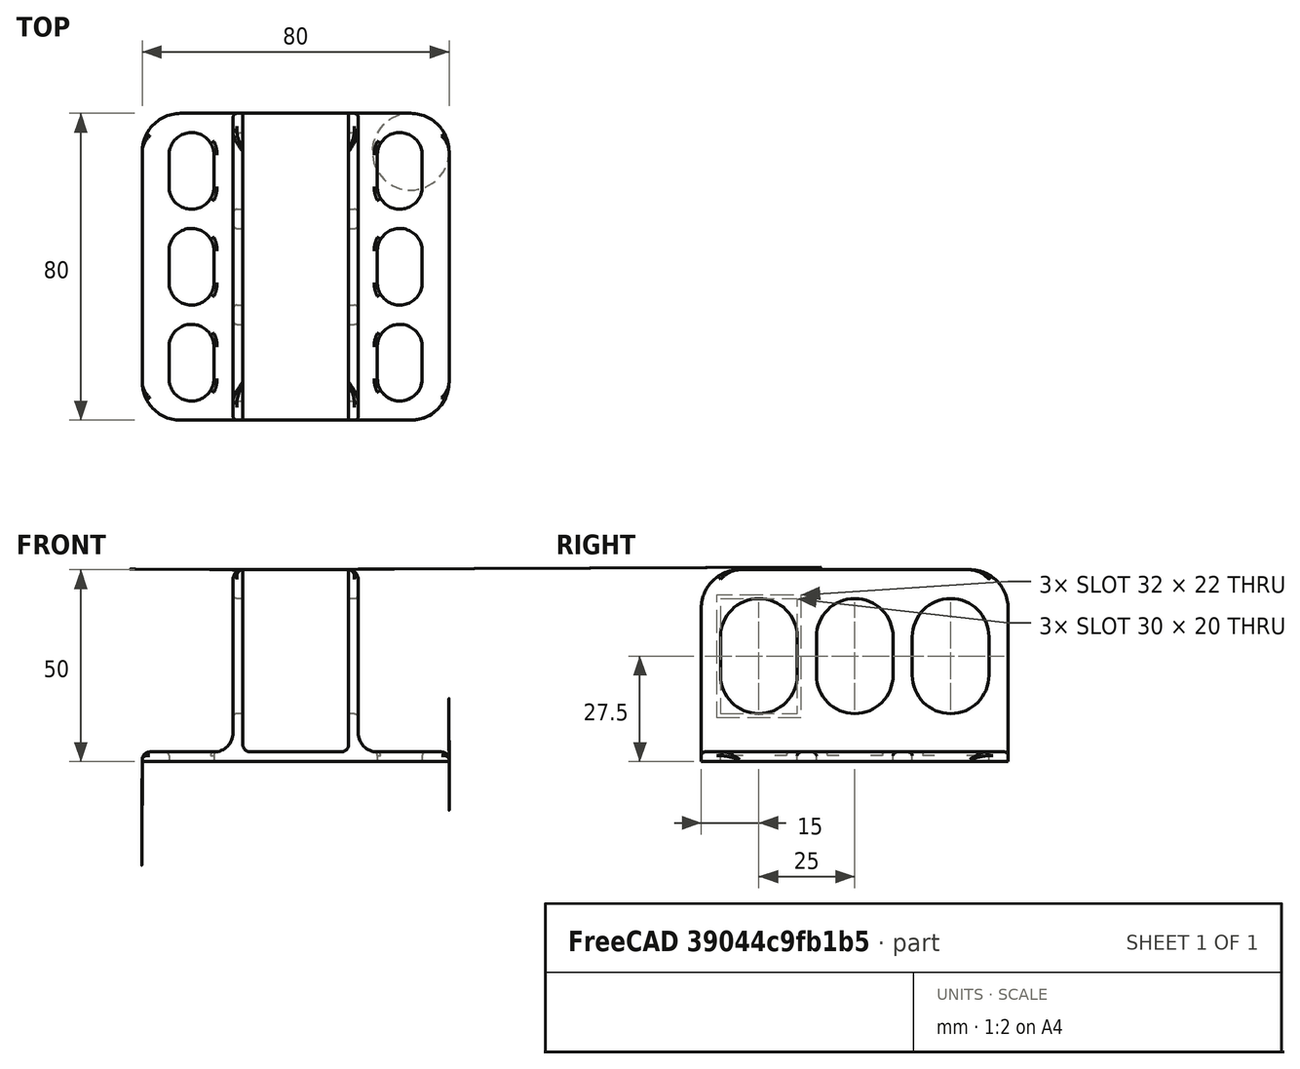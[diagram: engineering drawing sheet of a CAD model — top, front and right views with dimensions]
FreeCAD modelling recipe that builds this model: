
FCSTD DOCUMENT  (FreeCAD 1.0R39319 (Git))
Label: Charger Stand-2.1
License: Creative Commons Attribution 4.0
LicenseURL: https://creativecommons.org/licenses/by/4.0/
objects: Sketcher::SketchObject×5, PartDesign::Pocket×4, PartDesign::Pad×1, PartDesign::Fillet×1, PartDesign::Body×1
note: 29 computed .brp shape members not serialized (recipe doc carries the construction recipe); baked Part::Feature solids carry a one-line shape summary decoded from their .brp

FEATURE [Sketcher::SketchObject] Sketch
  ArcFitTolerance = 1e-06
  AttachmentSupport = -> [XZ_Plane]
  FullyConstrained = true
  MakeInternals = false
  MapMode = 5
  Placement = pos=(0,0,0) rot=(1,0,0;1.5708rad)
  sketch-geometry (18):
    g0: LineSegment StartX=-40 StartY=0 StartZ=0 EndX=40 EndY=0 EndZ=0
    g1: LineSegment StartX=38 StartY=2.5 StartZ=0 EndX=21.3 EndY=2.5 EndZ=0
    g2: LineSegment StartX=-38 StartY=2.5 StartZ=0 EndX=-21.3 EndY=2.5 EndZ=0
    g3: LineSegment StartX=-16.3 StartY=7.5 StartZ=0 EndX=-16.3 EndY=47.5 EndZ=0
    g4: LineSegment StartX=-13.8 StartY=50 StartZ=0 EndX=-13.8 EndY=4.5 EndZ=0
    g5: LineSegment StartX=-11.8 StartY=2.5 StartZ=0 EndX=11.8 EndY=2.5 EndZ=0
    g6: LineSegment StartX=13.8 StartY=4.5 StartZ=0 EndX=13.8 EndY=50 EndZ=0
    g7: LineSegment StartX=16.3 StartY=47.5 StartZ=0 EndX=16.3 EndY=7.5 EndZ=0
    g8: ArcOfCircle CenterX=-13.8 CenterY=47.5 CenterZ=0 NormalX=0 NormalY=0 NormalZ=1 AngleXU=0 Radius=2.5 StartAngle=1.5708 EndAngle=3.14159
    g9: ArcOfCircle CenterX=13.8 CenterY=47.5 CenterZ=0 NormalX=0 NormalY=0 NormalZ=1 AngleXU=0 Radius=2.5 StartAngle=-9e-16 EndAngle=1.5708
    g10: ArcOfCircle CenterX=21.3 CenterY=7.5 CenterZ=0 NormalX=0 NormalY=0 NormalZ=1 AngleXU=0 Radius=5 StartAngle=3.14159 EndAngle=4.71239
    g11: ArcOfCircle CenterX=11.8 CenterY=4.5 CenterZ=0 NormalX=0 NormalY=0 NormalZ=1 AngleXU=0 Radius=2 StartAngle=4.71239 EndAngle=6.28319
    g12: ArcOfCircle CenterX=-11.8 CenterY=4.5 CenterZ=0 NormalX=0 NormalY=0 NormalZ=1 AngleXU=0 Radius=2 StartAngle=3.14159 EndAngle=4.71239
    g13: ArcOfCircle CenterX=-21.3 CenterY=7.5 CenterZ=0 NormalX=0 NormalY=0 NormalZ=1 AngleXU=0 Radius=5 StartAngle=4.71239 EndAngle=6.28319
    g14: LineSegment StartX=40 StartY=0 StartZ=0 EndX=40 EndY=0.5 EndZ=0
    g15: LineSegment StartX=-40 StartY=0 StartZ=0 EndX=-40 EndY=0.5 EndZ=0
    g16: ArcOfCircle CenterX=38 CenterY=0.5 CenterZ=0 NormalX=0 NormalY=0 NormalZ=1 AngleXU=0 Radius=2 StartAngle=0 EndAngle=1.5708
    g17: ArcOfCircle CenterX=-38 CenterY=0.5 CenterZ=0 NormalX=0 NormalY=0 NormalZ=1 AngleXU=0 Radius=2 StartAngle=1.5708 EndAngle=3.14159
  constraints (47):
    c: PointOnObject(g0,g-1)
    c: Horizontal(g1)
    c: Horizontal(g2)
    c: Vertical(g3)
    c: Vertical(g4)
    c: Horizontal(g5)
    c: Vertical(g6)
    c: Vertical(g7)
    c: Coincident(g8,g4)
    c: Coincident(g9,g6)
    c: Symmetric(g0,g0,g-2)
    c: Tangent(g10,g1) = 1.5708
    c: Tangent(g10,g7) = -1.5708
    c: Tangent(g11,g6) = -1.5708
    c: Tangent(g11,g5) = -1.5708
    c: Tangent(g12,g5) = -1.5708
    c: Tangent(g12,g4) = -1.5708
    c: Tangent(g13,g3) = -1.5708
    c: Tangent(g13,g2) = -1.5708
    c: Tangent(g8,g3) = 1.5708
    c: Perpendicular(g8,g4)
    c: Perpendicular(g9,g6)
    c: Tangent(g9,g7) = 1.5708
    c: Coincident(g14,g0)
    c: Coincident(g15,g0)
    c: Vertical(g15)
    c: Tangent(g17,g15) = 1.5708
    c: Tangent(g17,g2) = 1.5708
    c: Tangent(g16,g14) = -1.5708
    c: Tangent(g16,g1) = -1.5708
    c: Vertical(g14)
    c: Equal(g14,g15)
    c: Equal(g17,g12)
    c: Equal(g12,g11)
    c: Equal(g11,g16)
    c: Equal(g8,g9)
    c: Equal(g2,g1)
    c: Equal(g7,g3)
    c: Equal(g4,g6)
    c: Radius(g16) = 2
    c: DistanceY(g1) = 2.5
    c: DistanceX(g4,g6) = 27.6
    c: Radius(g9) = 2.5
    c: Radius(g10) = 5
    c: Horizontal(g5,g1)
    c: DistanceY(g6) = 50
    c: DistanceX(g0,g0) = 80
FEATURE [PartDesign::Pad] Pad
  Direction = (0,-1,2e-16)
  Length = 80
  Length2 = 10
  Midplane = true
  Placement = pos=(0,0,0) rot=(1,0,0;1.5708rad)
  Profile = -> Sketch
  ReferenceAxis = -> Sketch [N_Axis]
  Refine = true
  Suppressed = false
  Type = 0
FEATURE [Sketcher::SketchObject] Sketch001
  ArcFitTolerance = 1e-06
  AttachmentSupport = -> [Pad]
  ExternalGeometry = -> [Pad]
  FullyConstrained = true
  MakeInternals = false
  MapMode = 5
  Placement = pos=(16.3,0,0) rot=(0.707107,0,0.707107;3.14159rad)
  sketch-geometry (6):
    g0: LineSegment StartX=50 StartY=40 StartZ=0 EndX=40 EndY=40 EndZ=0
    g1: LineSegment StartX=50 StartY=40 StartZ=0 EndX=50 EndY=30 EndZ=0
    g2: LineSegment StartX=50 StartY=-40 StartZ=0 EndX=50 EndY=-30 EndZ=0
    g3: LineSegment StartX=50 StartY=-40 StartZ=0 EndX=40 EndY=-40 EndZ=0
    g4: ArcOfCircle CenterX=40 CenterY=30 CenterZ=0 NormalX=0 NormalY=0 NormalZ=1 AngleXU=0 Radius=10 StartAngle=0 EndAngle=1.5708
    g5: ArcOfCircle CenterX=40 CenterY=-30 CenterZ=0 NormalX=0 NormalY=0 NormalZ=1 AngleXU=0 Radius=10 StartAngle=4.71239 EndAngle=6.28319
  constraints (17):
    c: Coincident(g0,g-3)
    c: Horizontal(g0)
    c: Coincident(g1,g0)
    c: PointOnObject(g1,g-3)
    c: Coincident(g2,g-3)
    c: PointOnObject(g2,g-3)
    c: Coincident(g3,g2)
    c: Horizontal(g3)
    c: Equal(g2,g3)
    c: Equal(g3,g1)
    c: Equal(g1,g0)
    c: Coincident(g4,g0)
    c: Coincident(g5,g2)
    c: Coincident(g5,g3)
    c: Tangent(g4,g1) = 1.5708
    c: Radius(g4) = 10
    c: Equal(g5,g4)
FEATURE [PartDesign::Pocket] Pocket
  BaseFeature = -> Pad
  Direction = (-1,0,2e-16)
  Length = 5
  Length2 = 5
  Placement = pos=(0,0,0) rot=(1,0,0;1.5708rad)
  Profile = -> Sketch001
  ReferenceAxis = -> Sketch001 [N_Axis]
  Refine = true
  Suppressed = false
  Type = 1
FEATURE [Sketcher::SketchObject] Sketch002
  ArcFitTolerance = 1e-06
  AttachmentSupport = -> [Pocket]
  ExternalGeometry = -> [Pocket]
  FullyConstrained = true
  MakeInternals = false
  MapMode = 5
  Placement = pos=(0,1.1e-15,2.5) rot=(0,0,1;3.14159rad)
  sketch-geometry (12):
    g0: LineSegment StartX=-40 StartY=30 StartZ=0 EndX=-40 EndY=40 EndZ=0
    g1: LineSegment StartX=-40 StartY=40 StartZ=0 EndX=-30 EndY=40 EndZ=0
    g2: LineSegment StartX=30 StartY=40 StartZ=0 EndX=40 EndY=40 EndZ=0
    g3: LineSegment StartX=40 StartY=40 StartZ=0 EndX=40 EndY=30 EndZ=0
    g4: LineSegment StartX=40 StartY=-30 StartZ=0 EndX=40 EndY=-40 EndZ=0
    g5: LineSegment StartX=40 StartY=-40 StartZ=0 EndX=30 EndY=-40 EndZ=0
    g6: LineSegment StartX=-40 StartY=-40 StartZ=0 EndX=-40 EndY=-30 EndZ=0
    g7: LineSegment StartX=-40 StartY=-40 StartZ=0 EndX=-30 EndY=-40 EndZ=0
    g8: ArcOfCircle CenterX=-30 CenterY=30 CenterZ=0 NormalX=0 NormalY=0 NormalZ=1 AngleXU=0 Radius=10 StartAngle=1.5708 EndAngle=3.14159
    g9: ArcOfCircle CenterX=30 CenterY=30 CenterZ=0 NormalX=0 NormalY=0 NormalZ=1 AngleXU=0 Radius=10 StartAngle=3e-16 EndAngle=1.5708
    g10: ArcOfCircle CenterX=30 CenterY=-30 CenterZ=0 NormalX=0 NormalY=0 NormalZ=1 AngleXU=0 Radius=10 StartAngle=4.71239 EndAngle=6.28319
    g11: ArcOfCircle CenterX=-30 CenterY=-30 CenterZ=0 NormalX=0 NormalY=0 NormalZ=1 AngleXU=0 Radius=10 StartAngle=3.14159 EndAngle=4.71239
  constraints (35):
    c: PointOnObject(g0,g-4)
    c: Coincident(g0,g-4)
    c: Coincident(g1,g0)
    c: Horizontal(g1)
    c: Coincident(g2,g-3)
    c: Horizontal(g2)
    c: Coincident(g3,g2)
    c: PointOnObject(g3,g-3)
    c: PointOnObject(g4,g-3)
    c: Coincident(g4,g-3)
    c: Coincident(g5,g4)
    c: Horizontal(g5)
    c: Coincident(g6,g-4)
    c: PointOnObject(g6,g-4)
    c: Coincident(g7,g6)
    c: Horizontal(g7)
    c: Equal(g7,g6)
    c: Equal(g6,g0)
    c: Equal(g0,g1)
    c: Equal(g1,g2)
    c: Equal(g2,g3)
    c: Equal(g3,g4)
    c: Equal(g4,g5)
    c: Coincident(g8,g0)
    c: Coincident(g8,g1)
    c: Coincident(g9,g2)
    c: Coincident(g9,g3)
    c: Coincident(g10,g5)
    c: Coincident(g11,g6)
    c: Coincident(g11,g7)
    c: Equal(g11,g8)
    c: Equal(g8,g9)
    c: Equal(g9,g10)
    c: Tangent(g10,g4) = 1.5708
    c: Radius(g9) = 10
FEATURE [PartDesign::Pocket] Pocket001
  BaseFeature = -> Pocket
  Direction = (0,0,-1)
  Length = 5
  Length2 = 5
  Placement = pos=(0,0,0) rot=(1,0,0;1.5708rad)
  Profile = -> Sketch002
  ReferenceAxis = -> Sketch002 [N_Axis]
  Refine = true
  Suppressed = false
  Type = 1
FEATURE [Sketcher::SketchObject] Sketch003
  ArcFitTolerance = 1e-06
  AttachmentSupport = -> [Pocket001]
  ExternalGeometry = -> [Pocket001]
  FullyConstrained = true
  MakeInternals = false
  MapMode = 5
  Placement = pos=(-16.3,0,0) rot=(0.707107,0,-0.707107;3.14159rad)
  sketch-geometry (17):
    g0: ArcOfCircle CenterX=-32.5 CenterY=25 CenterZ=0 NormalX=0 NormalY=0 NormalZ=1 AngleXU=0 Radius=10 StartAngle=1.5708 EndAngle=4.71239
    g1: ArcOfCircle CenterX=-22.5 CenterY=25 CenterZ=0 NormalX=0 NormalY=0 NormalZ=1 AngleXU=0 Radius=10 StartAngle=4.71239 EndAngle=7.85398
    g2: LineSegment StartX=-32.5 StartY=35 StartZ=0 EndX=-22.5 EndY=35 EndZ=0
    g3: LineSegment StartX=-32.5 StartY=15 StartZ=0 EndX=-22.5 EndY=15 EndZ=0
    g4: ArcOfCircle CenterX=-32.5 CenterY=0 CenterZ=0 NormalX=0 NormalY=0 NormalZ=1 AngleXU=0 Radius=10 StartAngle=1.5708 EndAngle=4.71239
    g5: ArcOfCircle CenterX=-22.5 CenterY=-9e-16 CenterZ=0 NormalX=0 NormalY=0 NormalZ=1 AngleXU=0 Radius=10 StartAngle=4.71239 EndAngle=7.85398
    g6: LineSegment StartX=-32.5 StartY=10 StartZ=0 EndX=-22.5 EndY=10 EndZ=0
    g7: LineSegment StartX=-32.5 StartY=-10 StartZ=0 EndX=-22.5 EndY=-10 EndZ=0
    g8: ArcOfCircle CenterX=-32.5 CenterY=-25 CenterZ=0 NormalX=0 NormalY=0 NormalZ=1 AngleXU=0 Radius=10 StartAngle=1.5708 EndAngle=4.71239
    g9: ArcOfCircle CenterX=-22.5 CenterY=-25 CenterZ=0 NormalX=0 NormalY=0 NormalZ=1 AngleXU=0 Radius=10 StartAngle=4.71239 EndAngle=7.85398
    g10: LineSegment StartX=-32.5 StartY=-15 StartZ=0 EndX=-22.5 EndY=-15 EndZ=0
    g11: LineSegment StartX=-32.5 StartY=-35 StartZ=0 EndX=-22.5 EndY=-35 EndZ=0
    g12: LineSegment [constr] StartX=-22.5 StartY=-9e-16 StartZ=0 EndX=-7.5 EndY=-9e-16 EndZ=0
    g13: LineSegment [constr] StartX=-32.5 StartY=0 StartZ=0 EndX=-47.5 EndY=0 EndZ=0
    g14: LineSegment [constr] StartX=-32.5 StartY=10 StartZ=0 EndX=-32.5 EndY=15 EndZ=0
    g15: LineSegment [constr] StartX=-32.5 StartY=35 StartZ=0 EndX=-32.5 EndY=40 EndZ=0
    g16: LineSegment [constr] StartX=-12.5 StartY=25 StartZ=0 EndX=-7.5 EndY=25 EndZ=0
  constraints (44):
    c: Tangent(g0,g2) = 1.5708
    c: Tangent(g0,g3) = -1.5708
    c: Tangent(g1,g2) = 1.5708
    c: Tangent(g1,g3) = -1.5708
    c: Equal(g0,g1)
    c: Horizontal(g2)
    c: Tangent(g4,g6) = 1.5708
    c: Tangent(g4,g7) = -1.5708
    c: Tangent(g5,g6) = 1.5708
    c: Tangent(g5,g7) = -1.5708
    c: Equal(g4,g5)
    c: Horizontal(g7)
    c: PointOnObject(g4,g-1)
    c: Tangent(g8,g10) = 1.5708
    c: Tangent(g8,g11) = -1.5708
    c: Tangent(g9,g10) = 1.5708
    c: Tangent(g9,g11) = -1.5708
    c: Equal(g8,g9)
    c: Equal(g5,g1)
    c: Equal(g1,g9)
    c: Vertical(g9,g5)
    c: Vertical(g8,g4)
    c: Vertical(g4,g0)
    c: Horizontal(g11)
    c: Coincident(g12,g5)
    c: PointOnObject(g12,g-5)
    c: Coincident(g13,g4)
    c: PointOnObject(g13,g-4)
    c: Coincident(g14,g4)
    c: Coincident(g14,g0)
    c: Coincident(g15,g0)
    c: PointOnObject(g15,g-3)
    c: Vertical(g15)
    c: Equal(g14,g15)
    c: Horizontal(g12)
    c: Horizontal(g13)
    c: Equal(g13,g12)
    c: Symmetric(g1,g9,g-1)
    c: DistanceY(g15,g15) = 5
    c: PointOnObject(g16,g1)
    c: PointOnObject(g16,g-5)
    c: Horizontal(g16)
    c: Perpendicular(g1,g16)
    c: Equal(g16,g15)
FEATURE [PartDesign::Pocket] Pocket002
  BaseFeature = -> Pocket001
  Direction = (1,0,2e-16)
  Length = 5
  Length2 = 5
  Placement = pos=(0,0,0) rot=(1,0,0;1.5708rad)
  Profile = -> Sketch003
  ReferenceAxis = -> Sketch003 [N_Axis]
  Refine = true
  Suppressed = false
  Type = 1
FEATURE [Sketcher::SketchObject] Sketch004
  ArcFitTolerance = 1e-06
  AttachmentSupport = -> [Pocket002]
  ExternalGeometry = -> [Pocket002]
  FullyConstrained = true
  MakeInternals = false
  MapMode = 5
  Placement = pos=(0,1.1e-15,2.5) rot=(0,0,1;3.14159rad)
  sketch-geometry (28):
    g0: ArcOfCircle CenterX=-27.15 CenterY=29.15 CenterZ=0 NormalX=0 NormalY=0 NormalZ=1 AngleXU=0 Radius=5.85 StartAngle=4e-16 EndAngle=3.14159
    g1: ArcOfCircle CenterX=-27.15 CenterY=20.85 CenterZ=0 NormalX=0 NormalY=0 NormalZ=1 AngleXU=0 Radius=5.85 StartAngle=3.14159 EndAngle=6.28319
    g2: LineSegment StartX=-21.3 StartY=29.15 StartZ=0 EndX=-21.3 EndY=20.85 EndZ=0
    g3: LineSegment StartX=-33 StartY=29.15 StartZ=0 EndX=-33 EndY=20.85 EndZ=0
    g4: ArcOfCircle CenterX=27.15 CenterY=29.15 CenterZ=0 NormalX=0 NormalY=0 NormalZ=1 AngleXU=0 Radius=5.85 StartAngle=0 EndAngle=3.14159
    g5: ArcOfCircle CenterX=27.15 CenterY=20.85 CenterZ=0 NormalX=0 NormalY=0 NormalZ=1 AngleXU=0 Radius=5.85 StartAngle=3.14159 EndAngle=6.28319
    g6: LineSegment StartX=33 StartY=29.15 StartZ=0 EndX=33 EndY=20.85 EndZ=0
    g7: LineSegment StartX=21.3 StartY=29.15 StartZ=0 EndX=21.3 EndY=20.85 EndZ=0
    g8: LineSegment [constr] StartX=33 StartY=29.15 StartZ=0 EndX=38 EndY=29.15 EndZ=0
    g9: LineSegment [constr] StartX=21.3 StartY=29.15 StartZ=0 EndX=16.3 EndY=29.15 EndZ=0
    g10: LineSegment [constr] StartX=27.15 StartY=35 StartZ=0 EndX=27.15 EndY=40 EndZ=0
    g11: ArcOfCircle CenterX=-27.15 CenterY=4.15 CenterZ=0 NormalX=0 NormalY=0 NormalZ=1 AngleXU=0 Radius=5.85 StartAngle=1e-16 EndAngle=3.14159
    g12: ArcOfCircle CenterX=-27.15 CenterY=-4.15 CenterZ=0 NormalX=0 NormalY=0 NormalZ=1 AngleXU=0 Radius=5.85 StartAngle=3.14159 EndAngle=6.28319
    g13: LineSegment StartX=-21.3 StartY=4.15 StartZ=0 EndX=-21.3 EndY=-4.15 EndZ=0
    g14: LineSegment StartX=-33 StartY=4.15 StartZ=0 EndX=-33 EndY=-4.15 EndZ=0
    g15: ArcOfCircle CenterX=-27.15 CenterY=-20.85 CenterZ=0 NormalX=0 NormalY=0 NormalZ=1 AngleXU=0 Radius=5.85 StartAngle=-9e-16 EndAngle=3.14159
    g16: ArcOfCircle CenterX=-27.15 CenterY=-29.15 CenterZ=0 NormalX=0 NormalY=0 NormalZ=1 AngleXU=0 Radius=5.85 StartAngle=3.14159 EndAngle=6.28319
    g17: LineSegment StartX=-21.3 StartY=-20.85 StartZ=0 EndX=-21.3 EndY=-29.15 EndZ=0
    g18: LineSegment StartX=-33 StartY=-20.85 StartZ=0 EndX=-33 EndY=-29.15 EndZ=0
    g19: ArcOfCircle CenterX=27.15 CenterY=4.15 CenterZ=0 NormalX=0 NormalY=0 NormalZ=1 AngleXU=0 Radius=5.85 StartAngle=1e-16 EndAngle=3.14159
    g20: ArcOfCircle CenterX=27.15 CenterY=-4.15 CenterZ=0 NormalX=0 NormalY=0 NormalZ=1 AngleXU=0 Radius=5.85 StartAngle=3.14159 EndAngle=6.28319
    g21: LineSegment StartX=33 StartY=4.15 StartZ=0 EndX=33 EndY=-4.15 EndZ=0
    g22: LineSegment StartX=21.3 StartY=4.15 StartZ=0 EndX=21.3 EndY=-4.15 EndZ=0
    g23: ArcOfCircle CenterX=27.15 CenterY=-20.85 CenterZ=0 NormalX=0 NormalY=0 NormalZ=1 AngleXU=0 Radius=5.85 StartAngle=0 EndAngle=3.14159
    g24: ArcOfCircle CenterX=27.15 CenterY=-29.15 CenterZ=0 NormalX=0 NormalY=0 NormalZ=1 AngleXU=0 Radius=5.85 StartAngle=3.14159 EndAngle=6.28319
    g25: LineSegment StartX=33 StartY=-20.85 StartZ=0 EndX=33 EndY=-29.15 EndZ=0
    g26: LineSegment StartX=21.3 StartY=-20.85 StartZ=0 EndX=21.3 EndY=-29.15 EndZ=0
    g27: LineSegment [constr] StartX=27.15 StartY=10 StartZ=0 EndX=27.15 EndY=15 EndZ=0
  constraints (67):
    c: Tangent(g0,g2) = 1.5708
    c: Tangent(g0,g3) = -1.5708
    c: Tangent(g1,g2) = 1.5708
    c: Tangent(g1,g3) = -1.5708
    c: Equal(g0,g1)
    c: Vertical(g3)
    c: Tangent(g4,g6) = 1.5708
    c: Tangent(g4,g7) = -1.5708
    c: Tangent(g5,g6) = 1.5708
    c: Tangent(g5,g7) = -1.5708
    c: Equal(g4,g5)
    c: Symmetric(g4,g0,g-2)
    c: Equal(g0,g4)
    c: Horizontal(g1,g5)
    c: Coincident(g8,g4)
    c: PointOnObject(g8,g-3)
    c: Coincident(g9,g4)
    c: PointOnObject(g9,g-4)
    c: Horizontal(g9)
    c: Horizontal(g8)
    c: PointOnObject(g10,g4)
    c: Vertical(g10)
    c: Perpendicular(g4,g10)
    c: Horizontal(g10,g-4)
    c: Equal(g9,g8)
    c: Equal(g8,g10)
    c: DistanceX(g8,g8) = 5
    c: Vertical(g7)
    c: Tangent(g11,g13) = 1.5708
    c: Tangent(g11,g14) = -1.5708
    c: Tangent(g12,g13) = 1.5708
    c: Tangent(g12,g14) = -1.5708
    c: Equal(g11,g12)
    c: Tangent(g15,g17) = 1.5708
    c: Tangent(g15,g18) = -1.5708
    c: Tangent(g16,g17) = 1.5708
    c: Tangent(g16,g18) = -1.5708
    c: Equal(g15,g16)
    c: Tangent(g19,g21) = 1.5708
    c: Tangent(g19,g22) = -1.5708
    c: Tangent(g20,g21) = 1.5708
    c: Tangent(g20,g22) = -1.5708
    c: Equal(g19,g20)
    c: Tangent(g23,g25) = 1.5708
    c: Tangent(g23,g26) = -1.5708
    c: Tangent(g24,g25) = 1.5708
    c: Tangent(g24,g26) = -1.5708
    c: Equal(g23,g24)
    c: Equal(g5,g19)
    c: Equal(g19,g11)
    c: Equal(g11,g15)
    c: Equal(g15,g23)
    c: Vertical(g25)
    c: Vertical(g15,g12)
    c: Symmetric(g19,g11,g-2)
    c: Symmetric(g20,g12,g-2)
    c: Symmetric(g15,g23,g-2)
    c: Symmetric(g16,g24,g-2)
    c: Symmetric(g20,g19,g-1)
    c: PointOnObject(g27,g19)
    c: PointOnObject(g27,g5)
    c: Vertical(g27)
    c: Perpendicular(g19,g27)
    c: Equal(g27,g8)
    c: Equal(g25,g21)
    c: Equal(g21,g6)
    c: Symmetric(g23,g5,g-1)
FEATURE [PartDesign::Pocket] Pocket003
  BaseFeature = -> Pocket002
  Direction = (0,0,-1)
  Length = 5
  Length2 = 5
  Placement = pos=(0,0,0) rot=(1,0,0;1.5708rad)
  Profile = -> Sketch004
  ReferenceAxis = -> Sketch004 [N_Axis]
  Refine = true
  Suppressed = false
  Type = 1
FEATURE [PartDesign::Fillet] Fillet
  Base = -> Pocket003 [Edge86,Edge85,Edge84,Edge69,Edge200,Edge196,Edge192,Edge82,Edge74,Edge140,Edge150,Edge146,Edge61,Edge130,Edge122,Edge114]
  BaseFeature = -> Pocket003
  Placement = pos=(0,0,0) rot=(1,0,0;1.5708rad)
  Radius = 1
  Refine = true
  SupportTransform = false
  Suppressed = false
  UseAllEdges = false
FEATURE [PartDesign::Body] Body  label="Charger Stand"
  AllowCompound = false
  Group = -> [Sketch,Pad,Sketch001,Pocket,Sketch002,Pocket001,Sketch003,Pocket002,Sketch004,Pocket003,Fillet]
  Origin = -> Origin
  Tip = -> Fillet
